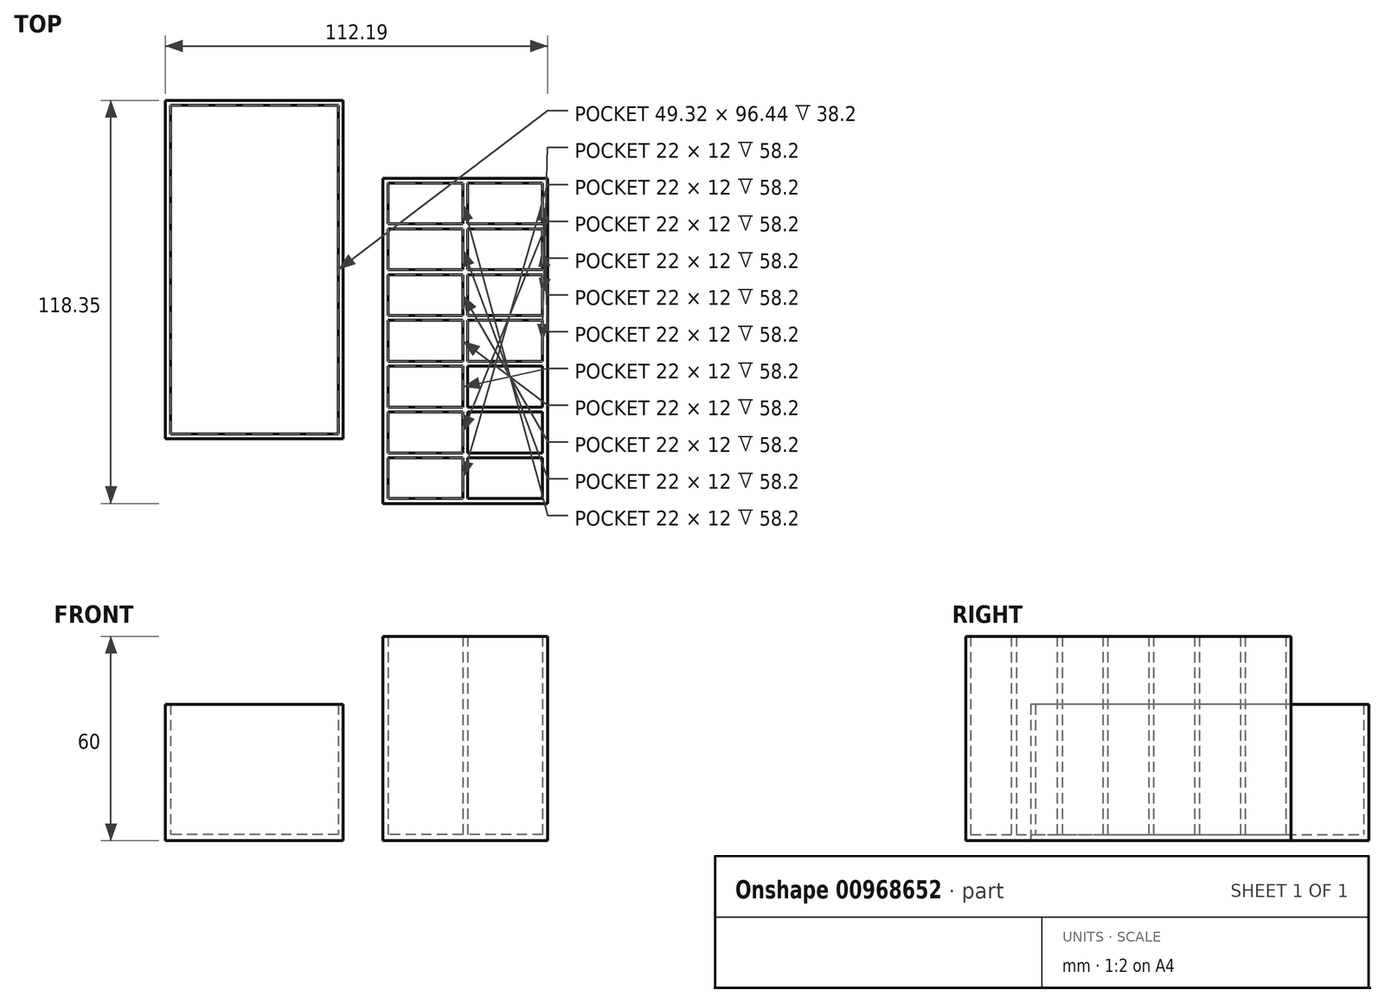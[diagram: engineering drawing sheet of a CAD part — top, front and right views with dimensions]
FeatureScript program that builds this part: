
annotation { "Feature Type Name" : "Feature", "Feature Type Description" : "" }
export const myFeature = defineFeature(function(context is Context, id is Id, definition is map)
    precondition{}
    {
        {
            var Q0;
            Q0=qCreatedBy(makeId("Top.planeOp"),FACE);
            var sketch = newSketch(context, id + "F0", { "sketchPlane" : qUnion([Q0])});
            skLineSegment(sketch, "E0.bottom", {"start": v(-32.1, 59.26) * mm, "end": v(16.23, 59.26) * mm});
            skLineSegment(sketch, "E0.top", {"start": v(-32.1, -36.26) * mm, "end": v(16.23, -36.26) * mm});
            skLineSegment(sketch, "E0.left", {"start": v(-32.1, 59.26) * mm, "end": v(-32.1, -36.26) * mm});
            skLineSegment(sketch, "E0.right", {"start": v(16.23, 59.26) * mm, "end": v(16.23, -36.26) * mm});
            skLineSegment(sketch, "E1.bottom", {"start": v(-30.65, 57.82) * mm, "end": v(-8.65, 57.82) * mm});
            skLineSegment(sketch, "E1.top", {"start": v(-30.65, 45.82) * mm, "end": v(-8.65, 45.82) * mm});
            skLineSegment(sketch, "E1.left", {"start": v(-30.65, 57.82) * mm, "end": v(-30.65, 45.82) * mm});
            skLineSegment(sketch, "E1.right", {"start": v(-8.65, 57.82) * mm, "end": v(-8.65, 45.82) * mm});
            skLineSegment(sketch, "E2.bottom", {"start": v(-30.65, 44.38) * mm, "end": v(-8.65, 44.38) * mm});
            skLineSegment(sketch, "E2.top", {"start": v(-30.65, 32.38) * mm, "end": v(-8.65, 32.38) * mm});
            skLineSegment(sketch, "E2.left", {"start": v(-30.65, 44.38) * mm, "end": v(-30.65, 32.38) * mm});
            skLineSegment(sketch, "E2.right", {"start": v(-8.65, 44.38) * mm, "end": v(-8.65, 32.38) * mm});
            skLineSegment(sketch, "E3.bottom", {"start": v(-30.65, 30.94) * mm, "end": v(-8.65, 30.94) * mm});
            skLineSegment(sketch, "E3.top", {"start": v(-30.65, 18.94) * mm, "end": v(-8.65, 18.94) * mm});
            skLineSegment(sketch, "E3.left", {"start": v(-30.65, 30.94) * mm, "end": v(-30.65, 18.94) * mm});
            skLineSegment(sketch, "E3.right", {"start": v(-8.65, 30.94) * mm, "end": v(-8.65, 18.94) * mm});
            skLineSegment(sketch, "E4.bottom", {"start": v(-30.65, 17.5) * mm, "end": v(-8.65, 17.5) * mm});
            skLineSegment(sketch, "E4.top", {"start": v(-30.65, 5.5) * mm, "end": v(-8.65, 5.5) * mm});
            skLineSegment(sketch, "E4.left", {"start": v(-30.65, 17.5) * mm, "end": v(-30.65, 5.5) * mm});
            skLineSegment(sketch, "E4.right", {"start": v(-8.65, 17.5) * mm, "end": v(-8.65, 5.5) * mm});
            skLineSegment(sketch, "E5.bottom", {"start": v(-30.65, 4.06) * mm, "end": v(-8.65, 4.06) * mm});
            skLineSegment(sketch, "E5.top", {"start": v(-30.65, -7.94) * mm, "end": v(-8.65, -7.94) * mm});
            skLineSegment(sketch, "E5.left", {"start": v(-30.65, 4.06) * mm, "end": v(-30.65, -7.94) * mm});
            skLineSegment(sketch, "E5.right", {"start": v(-8.65, 4.06) * mm, "end": v(-8.65, -7.94) * mm});
            skLineSegment(sketch, "E6.bottom", {"start": v(-7.21, 57.82) * mm, "end": v(14.79, 57.82) * mm});
            skLineSegment(sketch, "E6.top", {"start": v(-7.21, 45.82) * mm, "end": v(14.79, 45.82) * mm});
            skLineSegment(sketch, "E6.left", {"start": v(-7.21, 57.82) * mm, "end": v(-7.21, 45.82) * mm});
            skLineSegment(sketch, "E6.right", {"start": v(14.79, 57.82) * mm, "end": v(14.79, 45.82) * mm});
            skLineSegment(sketch, "E7.bottom", {"start": v(-7.21, 44.38) * mm, "end": v(14.79, 44.38) * mm});
            skLineSegment(sketch, "E7.top", {"start": v(-7.21, 32.38) * mm, "end": v(14.79, 32.38) * mm});
            skLineSegment(sketch, "E7.left", {"start": v(-7.21, 44.38) * mm, "end": v(-7.21, 32.38) * mm});
            skLineSegment(sketch, "E7.right", {"start": v(14.79, 44.38) * mm, "end": v(14.79, 32.38) * mm});
            skLineSegment(sketch, "E8.bottom", {"start": v(-7.21, 30.94) * mm, "end": v(14.79, 30.94) * mm});
            skLineSegment(sketch, "E8.top", {"start": v(-7.21, 18.94) * mm, "end": v(14.79, 18.94) * mm});
            skLineSegment(sketch, "E8.left", {"start": v(-7.21, 30.94) * mm, "end": v(-7.21, 18.94) * mm});
            skLineSegment(sketch, "E8.right", {"start": v(14.79, 30.94) * mm, "end": v(14.79, 18.94) * mm});
            skLineSegment(sketch, "E9.bottom", {"start": v(-30.65, -9.38) * mm, "end": v(-8.65, -9.38) * mm});
            skLineSegment(sketch, "E9.top", {"start": v(-30.65, -21.38) * mm, "end": v(-8.65, -21.38) * mm});
            skLineSegment(sketch, "E9.left", {"start": v(-30.65, -9.38) * mm, "end": v(-30.65, -21.38) * mm});
            skLineSegment(sketch, "E9.right", {"start": v(-8.65, -9.38) * mm, "end": v(-8.65, -21.38) * mm});
            skLineSegment(sketch, "E10.bottom", {"start": v(-30.65, -22.82) * mm, "end": v(-8.65, -22.82) * mm});
            skLineSegment(sketch, "E10.top", {"start": v(-30.65, -34.82) * mm, "end": v(-8.65, -34.82) * mm});
            skLineSegment(sketch, "E10.left", {"start": v(-30.65, -22.82) * mm, "end": v(-30.65, -34.82) * mm});
            skLineSegment(sketch, "E10.right", {"start": v(-8.65, -22.82) * mm, "end": v(-8.65, -34.82) * mm});
            skLineSegment(sketch, "E11.bottom", {"start": v(-7.21, 17.5) * mm, "end": v(14.79, 17.5) * mm});
            skLineSegment(sketch, "E11.top", {"start": v(-7.21, 5.5) * mm, "end": v(14.79, 5.5) * mm});
            skLineSegment(sketch, "E11.left", {"start": v(-7.21, 17.5) * mm, "end": v(-7.21, 5.5) * mm});
            skLineSegment(sketch, "E11.right", {"start": v(14.79, 17.5) * mm, "end": v(14.79, 5.5) * mm});
            skLineSegment(sketch, "E12.bottom", {"start": v(-7.21, 4.06) * mm, "end": v(14.79, 4.06) * mm});
            skLineSegment(sketch, "E12.top", {"start": v(-7.21, -7.94) * mm, "end": v(14.79, -7.94) * mm});
            skLineSegment(sketch, "E12.left", {"start": v(-7.21, 4.06) * mm, "end": v(-7.21, -7.94) * mm});
            skLineSegment(sketch, "E12.right", {"start": v(14.79, 4.06) * mm, "end": v(14.79, -7.94) * mm});
            skLineSegment(sketch, "E13.bottom", {"start": v(-7.21, -9.38) * mm, "end": v(14.79, -9.38) * mm});
            skLineSegment(sketch, "E13.top", {"start": v(-7.21, -21.38) * mm, "end": v(14.79, -21.38) * mm});
            skLineSegment(sketch, "E13.left", {"start": v(-7.21, -9.38) * mm, "end": v(-7.21, -21.38) * mm});
            skLineSegment(sketch, "E13.right", {"start": v(14.79, -9.38) * mm, "end": v(14.79, -21.38) * mm});
            skLineSegment(sketch, "E14.bottom", {"start": v(-7.21, -22.82) * mm, "end": v(14.79, -22.82) * mm});
            skLineSegment(sketch, "E14.top", {"start": v(-7.21, -34.82) * mm, "end": v(14.79, -34.82) * mm});
            skLineSegment(sketch, "E14.left", {"start": v(-7.21, -22.82) * mm, "end": v(-7.21, -34.82) * mm});
            skLineSegment(sketch, "E14.right", {"start": v(14.79, -22.82) * mm, "end": v(14.79, -34.82) * mm});
            skSolve(sketch);
        }
        {
            var Q0;
            Q0=makeQuery(id+"F0.imprint","IMPRINT",FACE,{"disambiguationData":[TD([[makeQuery(id+"F0.imprint","IMPRINT",EDGE,{"derivedFrom":sQuery(id+"F0.wireOp",EDGE,"E1.bottom")}),-1.0]])]});
            var Q1;
            Q1=makeQuery(id+"F0.imprint","IMPRINT",FACE,{"disambiguationData":[TD([[makeQuery(id+"F0.imprint","IMPRINT",EDGE,{"derivedFrom":sQuery(id+"F0.wireOp",EDGE,"E0.bottom")}),-1.0]])]});
            var Q2;
            Q2=makeQuery(id+"F0.imprint","IMPRINT",FACE,{"disambiguationData":[TD([[makeQuery(id+"F0.imprint","IMPRINT",EDGE,{"derivedFrom":sQuery(id+"F0.wireOp",EDGE,"E3.bottom")}),-1.0]])]});
            var Q3;
            Q3=makeQuery(id+"F0.imprint","IMPRINT",FACE,{"disambiguationData":[TD([[makeQuery(id+"F0.imprint","IMPRINT",EDGE,{"derivedFrom":sQuery(id+"F0.wireOp",EDGE,"E12.bottom")}),-1.0]])]});
            var Q4;
            Q4=makeQuery(id+"F0.imprint","IMPRINT",FACE,{"disambiguationData":[TD([[makeQuery(id+"F0.imprint","IMPRINT",EDGE,{"derivedFrom":sQuery(id+"F0.wireOp",EDGE,"E13.bottom")}),-1.0]])]});
            var Q5;
            Q5=makeQuery(id+"F0.imprint","IMPRINT",FACE,{"disambiguationData":[TD([[makeQuery(id+"F0.imprint","IMPRINT",EDGE,{"derivedFrom":sQuery(id+"F0.wireOp",EDGE,"E11.bottom")}),-1.0]])]});
            var Q6;
            Q6=makeQuery(id+"F0.imprint","IMPRINT",FACE,{"disambiguationData":[TD([[makeQuery(id+"F0.imprint","IMPRINT",EDGE,{"derivedFrom":sQuery(id+"F0.wireOp",EDGE,"E9.bottom")}),-1.0]])]});
            var Q7;
            Q7=makeQuery(id+"F0.imprint","IMPRINT",FACE,{"disambiguationData":[TD([[makeQuery(id+"F0.imprint","IMPRINT",EDGE,{"derivedFrom":sQuery(id+"F0.wireOp",EDGE,"E7.bottom")}),-1.0]])]});
            var Q8;
            Q8=makeQuery(id+"F0.imprint","IMPRINT",FACE,{"disambiguationData":[TD([[makeQuery(id+"F0.imprint","IMPRINT",EDGE,{"derivedFrom":sQuery(id+"F0.wireOp",EDGE,"E5.bottom")}),-1.0]])]});
            var Q9;
            Q9=makeQuery(id+"F0.imprint","IMPRINT",FACE,{"disambiguationData":[TD([[makeQuery(id+"F0.imprint","IMPRINT",EDGE,{"derivedFrom":sQuery(id+"F0.wireOp",EDGE,"E4.bottom")}),-1.0]])]});
            var Q10;
            Q10=makeQuery(id+"F0.imprint","IMPRINT",FACE,{"disambiguationData":[TD([[makeQuery(id+"F0.imprint","IMPRINT",EDGE,{"derivedFrom":sQuery(id+"F0.wireOp",EDGE,"E14.bottom")}),-1.0]])]});
            var Q11;
            Q11=makeQuery(id+"F0.imprint","IMPRINT",FACE,{"disambiguationData":[TD([[makeQuery(id+"F0.imprint","IMPRINT",EDGE,{"derivedFrom":sQuery(id+"F0.wireOp",EDGE,"E10.bottom")}),-1.0]])]});
            var Q12;
            Q12=makeQuery(id+"F0.imprint","IMPRINT",FACE,{"disambiguationData":[TD([[makeQuery(id+"F0.imprint","IMPRINT",EDGE,{"derivedFrom":sQuery(id+"F0.wireOp",EDGE,"E6.bottom")}),-1.0]])]});
            var Q13;
            Q13=makeQuery(id+"F0.imprint","IMPRINT",FACE,{"disambiguationData":[TD([[makeQuery(id+"F0.imprint","IMPRINT",EDGE,{"derivedFrom":sQuery(id+"F0.wireOp",EDGE,"E2.bottom")}),-1.0]])]});
            var Q14;
            Q14=makeQuery(id+"F0.imprint","IMPRINT",FACE,{"disambiguationData":[TD([[makeQuery(id+"F0.imprint","IMPRINT",EDGE,{"derivedFrom":sQuery(id+"F0.wireOp",EDGE,"E8.bottom")}),-1.0]])]});
            extrude(context, id + "F1", {"entities" : qUnion([Q0, Q1, Q2, Q3, Q4, Q5, Q6, Q7, Q8, Q9, Q10, Q11, Q12, Q13, Q14]), "depth" : 1.8 * mm, "offsetDistance" : 25 * mm});
        }
        {
            var Q0;
            Q0=makeQuery(id+"F0.imprint","IMPRINT",FACE,{"disambiguationData":[TD([[makeQuery(id+"F0.imprint","IMPRINT",EDGE,{"derivedFrom":sQuery(id+"F0.wireOp",EDGE,"E0.bottom")}),-1.0]])]});
            extrude(context, id + "F2", {"entities" : qUnion([Q0]), "operationType" : NewBodyOperationType.ADD, "depth" : 60 * mm, "offsetDistance" : 25 * mm});
        }
        {
            var Q0;
            Q0=qCreatedBy(makeId("Top.planeOp"),FACE);
            var sketch = newSketch(context, id + "F3", { "sketchPlane" : qUnion([Q0])});
            skLineSegment(sketch, "E15.bottom", {"start": v(-95.96, 82.09) * mm, "end": v(-43.76, 82.09) * mm});
            skLineSegment(sketch, "E15.top", {"start": v(-95.96, -17.23) * mm, "end": v(-43.76, -17.23) * mm});
            skLineSegment(sketch, "E15.left", {"start": v(-95.96, 82.09) * mm, "end": v(-95.96, -17.23) * mm});
            skLineSegment(sketch, "E15.right", {"start": v(-43.76, 82.09) * mm, "end": v(-43.76, -17.23) * mm});
            skLineSegment(sketch, "E16.bottom", {"start": v(-94.52, 80.65) * mm, "end": v(-45.2, 80.65) * mm});
            skLineSegment(sketch, "E16.top", {"start": v(-94.52, -15.8) * mm, "end": v(-45.2, -15.8) * mm});
            skLineSegment(sketch, "E16.left", {"start": v(-94.52, 80.65) * mm, "end": v(-94.52, -15.8) * mm});
            skLineSegment(sketch, "E16.right", {"start": v(-45.2, 80.65) * mm, "end": v(-45.2, -15.8) * mm});
            skSolve(sketch);
        }
        {
            var Q0;
            Q0=makeQuery(id+"F3.imprint","IMPRINT",FACE,{"disambiguationData":[TD([[makeQuery(id+"F3.imprint","IMPRINT",EDGE,{"derivedFrom":sQuery(id+"F3.wireOp",EDGE,"E16.bottom")}),-1.0]])]});
            var Q1;
            Q1=makeQuery(id+"F3.imprint","IMPRINT",FACE,{"disambiguationData":[TD([[makeQuery(id+"F3.imprint","IMPRINT",EDGE,{"derivedFrom":sQuery(id+"F3.wireOp",EDGE,"E15.bottom")}),-1.0]])]});
            extrude(context, id + "F4", {"entities" : qUnion([Q0, Q1]), "depth" : 1.8 * mm, "offsetDistance" : 25 * mm});
        }
        {
            var Q0;
            Q0=makeQuery(id+"F3.imprint","IMPRINT",FACE,{"disambiguationData":[TD([[makeQuery(id+"F3.imprint","IMPRINT",EDGE,{"derivedFrom":sQuery(id+"F3.wireOp",EDGE,"E15.bottom")}),-1.0]])]});
            extrude(context, id + "F5", {"entities" : qUnion([Q0]), "operationType" : NewBodyOperationType.ADD, "depth" : 40 * mm, "offsetDistance" : 25 * mm});
        }
    });
